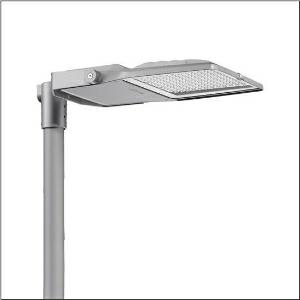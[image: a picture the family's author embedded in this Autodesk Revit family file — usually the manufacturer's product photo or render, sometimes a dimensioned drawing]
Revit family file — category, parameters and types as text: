
# Revit family: floodlight_fl_21_iq_midi___pl61_5xa7782e2c3a_85c4
name_source: partatom
category: Lighting Fixtures
units: mm (PartAtom-declared; Revit-internal decimal feet)

## family parameters
Cut with Voids When Loaded = No
Host = Face
Light Source = No
Part Type = Normal
Room Calculation Point = No
Round Connector Dimension = Use Diameter
Shared = No

## types (1)
- --- (1 x LED, 26360 lm, 208.1 W, 3000K)
    Apparent Load = 208 VA
    CIE Flux Codes = 33 65 98 100 100
    Color Rendering = 70
    Color Temperature = 3000K
    Default Elevation = 1800 mm
    Description = Floodlight FL 21 iQ midi, floodlight, primary light control with lens, of PMMA, primary optical cover: protective disc, of toughened safety glass, transparent, light distribution: PL61, light emission: direct distribution, installation type: surface-mounted, LED, High Power LED, rated luminous flux: 26.360lm, luminous efficacy: 127lm/W, light colour: 730, colour temperature: 3000K, control gear: iQ Street-Remote/DALI, control: optimised constant luminous flux control (CLO 2.0), Desk-Remote (wireless, voltage-free reading and setting of iQ features in the workshop via application-optimized NFC function/RFID function), Smart-Wire, Night-Set, Temp-Guard, Auto-Match, Street-Remote, with terminal, 6-pole, mains connection: 220..240V, AC, 50/60Hz, start of lifetime: 208W, end of service life: 227W, reduction: 90W, luminaire housing, of diecast aluminium, powder-coated, Siteco® metallic grey (DB 702S), corrosivity category C5 mid according to DIN EN ISO 12944, suitable for swimming pools, chlorine-resistant, sealing non-destructively replaceable, please order mast flange separately, mast bracket, of steel, galvanised, powder-coated, Siteco® metallic grey (DB 702S), protection rating (complete): IP66, insulation class (complete): insulation class II (safety insulation), certification: CE, ENEC, VDE, protection symbol: D, impact resistance: IK08, permissible operating ambient temperature: -40..+40°C, permissible operating ambient temperature for outdoor applications: -40..+50°C, standard: DIN EN 12944, LABS conformity tested according to VDMA 24364:2018-05, packaging unit: 1 piece

Light Distribution: PL61
    Height = 76 mm
    Lamp = 1 x LED
    Lamp Light Flux = 26360 lm
    Lamp Power = 208.1 W
    Lamp count = 1
    Length = 657 mm
    Luminous efficacy = 127 lm/W
    Manufacturer = Siteco
    ModVariant = No
    Model = 5XA7782E2C3A
    Number of Poles = 1
    OnlyDefault = Yes
    Power Factor = 1
    Product Name = Floodlight FL 21 iQ midi | PL61
    Product group = floodlight | pylon annexe
    ProductGroupID = 6201
    Protection Class = Protection class II
    Protection Degree = IP 66
    RLX_Detail_Level = 1
    RLX_Emergency_Light_Flux = 0 lm
    RLX_Emergency_Type = 0
    RLX_Emergency_Type_DB = No
    RlxData = <blob elided: 153905 chars, md5=74d6729f>
    Socket = socket
    Standby Power = 0 W
    System Light Flux = 26360 lm
    System Power = 208 W
    Type Comments = factory setting: luminous flux: 100 % | dim-lin: 254 | 710 mA
    Type Image = l_1007123.jpg
    URL = http://relux.com
    VarID = @adj_130181
    Voltage = 0 V
    Weight = 0.00 kg
    Width = 442 mm

## geometry (parser evidence)
native form markers: Blend x4, Sweep x14
no freeform markers — native parametric forms only
